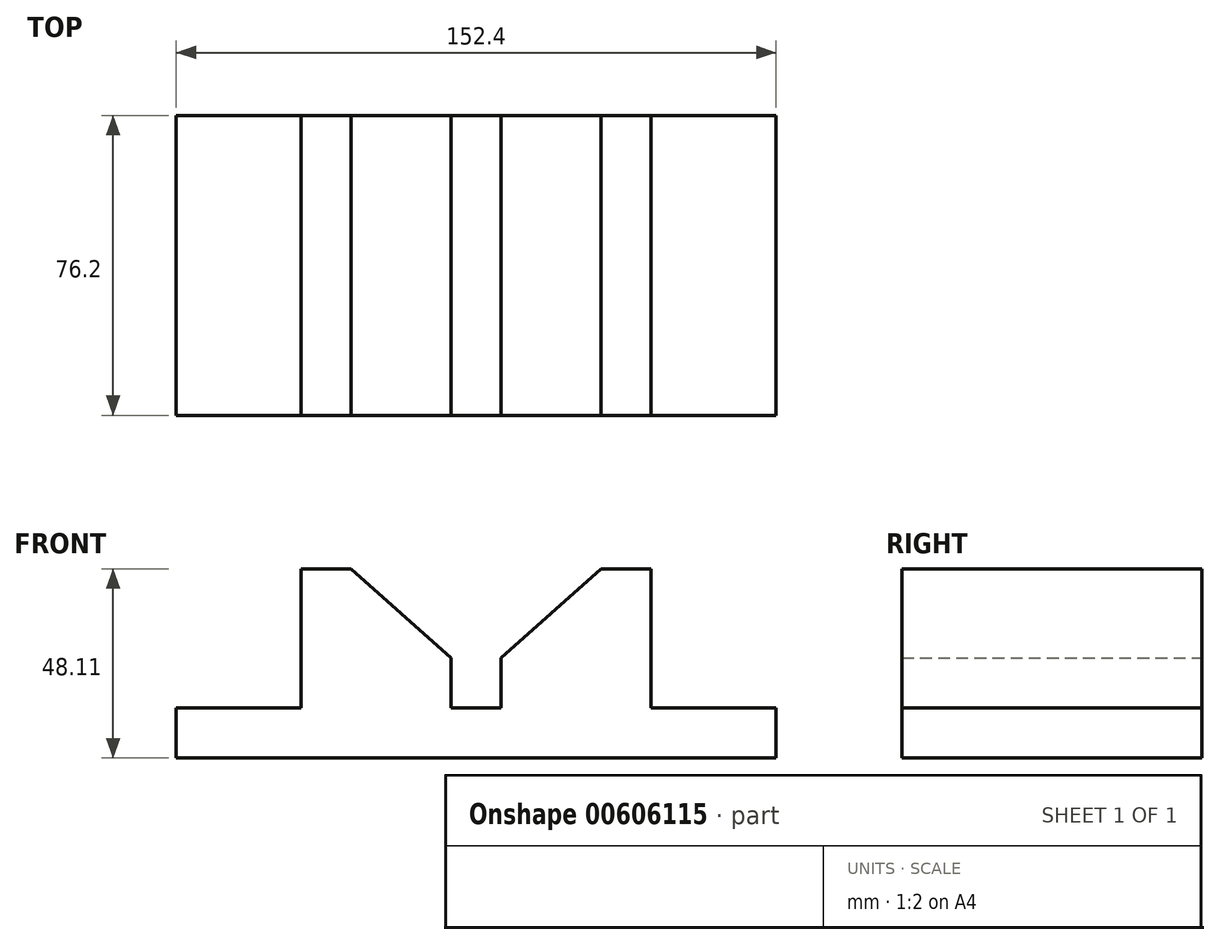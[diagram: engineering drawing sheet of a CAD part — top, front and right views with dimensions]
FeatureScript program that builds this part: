
annotation { "Feature Type Name" : "Feature", "Feature Type Description" : "" }
export const myFeature = defineFeature(function(context is Context, id is Id, definition is map)
    precondition{}
    {
        {
            var Q0;
            Q0=qCreatedBy(makeId("Front.planeOp"),FACE);
            var sketch = newSketch(context, id + "F0", { "sketchPlane" : qUnion([Q0])});
            skLineSegment(sketch, "E0", {"start": v(-56.86, 0) * mm, "end": v(-56.86, 12.7) * mm});
            skLineSegment(sketch, "E1", {"start": v(-56.86, 12.7) * mm, "end": v(-25.1, 12.7) * mm});
            skLineSegment(sketch, "E2", {"start": v(-25.1, 12.7) * mm, "end": v(-25.1, 48.11) * mm});
            skLineSegment(sketch, "E3", {"start": v(-25.1, 48.11) * mm, "end": v(-12.4, 48.11) * mm});
            skLineSegment(sketch, "E4", {"start": v(51.1, 48.11) * mm, "end": v(63.8, 48.11) * mm});
            skLineSegment(sketch, "E5", {"start": v(63.8, 48.11) * mm, "end": v(63.8, 12.7) * mm});
            skLineSegment(sketch, "E6", {"start": v(63.8, 12.7) * mm, "end": v(95.54, 12.7) * mm});
            skLineSegment(sketch, "E7", {"start": v(95.54, 12.7) * mm, "end": v(95.54, 0) * mm});
            skLineSegment(sketch, "E8", {"start": v(-56.86, 0) * mm, "end": v(95.54, 0) * mm});
            skLineSegment(sketch, "E9", {"start": v(19.34, 12.7) * mm, "end": v(25.7, 12.7) * mm});
            skLineSegment(sketch, "E10", {"start": v(25.7, 12.7) * mm, "end": v(25.7, 25.4) * mm});
            skLineSegment(sketch, "E11", {"start": v(19.34, 12.7) * mm, "end": v(13, 12.7) * mm});
            skLineSegment(sketch, "E12", {"start": v(13, 12.7) * mm, "end": v(13, 25.4) * mm});
            skLineSegment(sketch, "E13", {"start": v(25.7, 25.4) * mm, "end": v(51.1, 48.11) * mm});
            skLineSegment(sketch, "E14", {"start": v(-12.4, 48.11) * mm, "end": v(13, 25.4) * mm});
            skSolve(sketch);
        }
        {
            var Q0;
            Q0=makeQuery(id+"F0.imprint","IMPRINT",FACE,{"disambiguationData":[TD([[makeQuery(id+"F0.imprint","IMPRINT",EDGE,{"derivedFrom":sQuery(id+"F0.wireOp",EDGE,"E0")}),-1.0]])]});
            extrude(context, id + "F1", {"entities" : qUnion([Q0]), "depth" : 76.2 * mm, "offsetDistance" : 25.4 * mm});
        }
    });
